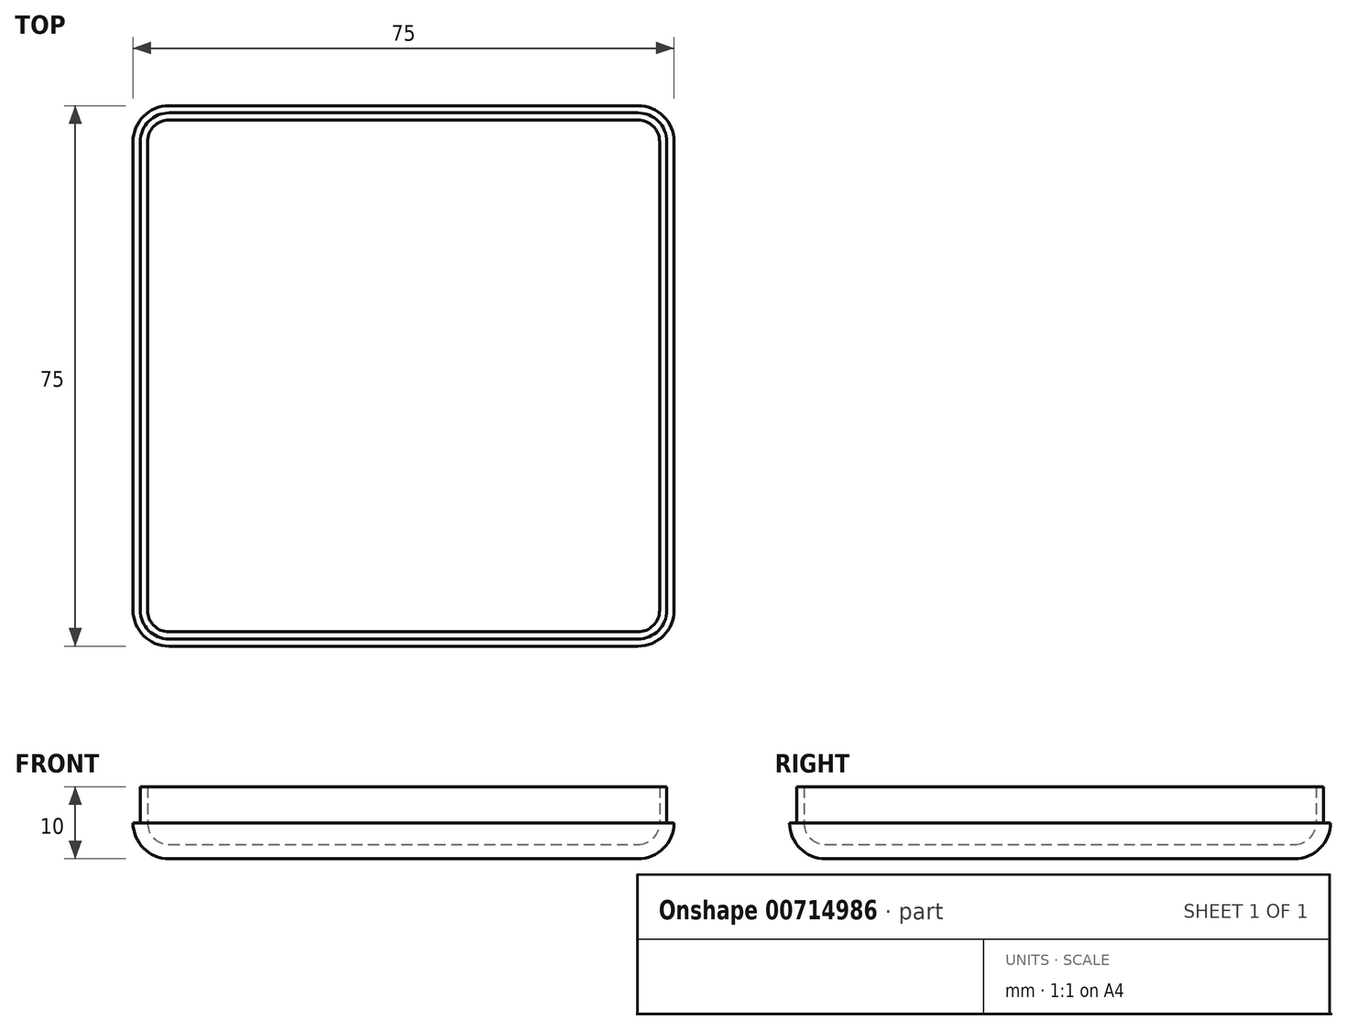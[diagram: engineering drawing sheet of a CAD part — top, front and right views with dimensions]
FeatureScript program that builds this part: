
annotation { "Feature Type Name" : "Feature", "Feature Type Description" : "" }
export const myFeature = defineFeature(function(context is Context, id is Id, definition is map)
    precondition{}
    {
        {
            var Q0;
            Q0=qCreatedBy(makeId("Top.planeOp"),FACE);
            var sketch = newSketch(context, id + "F0", { "sketchPlane" : qUnion([Q0])});
            skLineSegment(sketch, "E0.bottom", {"start": v(-37.5, 37.5) * mm, "end": v(37.5, 37.5) * mm});
            skLineSegment(sketch, "E0.top", {"start": v(-37.5, -37.5) * mm, "end": v(37.5, -37.5) * mm});
            skLineSegment(sketch, "E0.left", {"start": v(-37.5, 37.5) * mm, "end": v(-37.5, -37.5) * mm});
            skLineSegment(sketch, "E0.right", {"start": v(37.5, 37.5) * mm, "end": v(37.5, -37.5) * mm});
            skPoint(sketch, "E0.middle", {"position": v(0, 0) * mm});
            skLineSegment(sketch, "E1.0", {"start": v(-35.5, 35.5) * mm, "end": v(35.5, 35.5) * mm});
            skLineSegment(sketch, "E1.1", {"start": v(-35.5, 35.5) * mm, "end": v(-35.5, -35.5) * mm});
            skLineSegment(sketch, "E1.2", {"start": v(-35.5, -35.5) * mm, "end": v(35.5, -35.5) * mm});
            skLineSegment(sketch, "E1.3", {"start": v(35.5, 35.5) * mm, "end": v(35.5, -35.5) * mm});
            skSolve(sketch);
        }
        {
            var Q0;
            Q0=makeQuery(id+"F0.imprint","IMPRINT",FACE,{"disambiguationData":[TD([[makeQuery(id+"F0.imprint","IMPRINT",EDGE,{"derivedFrom":sQuery(id+"F0.wireOp",EDGE,"E1.0")}),-1.0]])]});
            var Q1;
            Q1=makeQuery(id+"F0.imprint","IMPRINT",FACE,{"disambiguationData":[TD([[makeQuery(id+"F0.imprint","IMPRINT",EDGE,{"derivedFrom":sQuery(id+"F0.wireOp",EDGE,"E0.bottom")}),-1.0]])]});
            extrude(context, id + "F1", {"entities" : qUnion([Q0, Q1]), "depth" : 5 * mm, "offsetDistance" : 25 * mm});
        }
        {
            var Q0;
            Q0=makeQuery(id+"F1.opExtrude","SWEPT_EDGE",EDGE,{"disambiguationData":[OSD([sQuery(id+"F0.wireOp",EDGE,"E0.top"),sQuery(id+"F0.wireOp",EDGE,"E0.left")])]});
            var Q1;
            Q1=makeQuery(id+"F1.opExtrude","SWEPT_EDGE",EDGE,{"disambiguationData":[OSD([sQuery(id+"F0.wireOp",EDGE,"E0.top"),sQuery(id+"F0.wireOp",EDGE,"E0.right")])]});
            var Q2;
            Q2=makeQuery(id+"F1.opExtrude","CAP_EDGE",EDGE,{"disambiguationData":[OSD([sQuery(id+"F0.wireOp",EDGE,"E0.top")])],"isStart":true});
            var Q3;
            Q3=makeQuery(id+"F1.opExtrude","CAP_EDGE",EDGE,{"disambiguationData":[OSD([sQuery(id+"F0.wireOp",EDGE,"E0.left")])],"isStart":true});
            var Q4;
            Q4=makeQuery(id+"F1.opExtrude","SWEPT_EDGE",EDGE,{"disambiguationData":[OSD([sQuery(id+"F0.wireOp",EDGE,"E0.bottom"),sQuery(id+"F0.wireOp",EDGE,"E0.left")])]});
            var Q5;
            Q5=makeQuery(id+"F1.opExtrude","CAP_EDGE",EDGE,{"disambiguationData":[OSD([sQuery(id+"F0.wireOp",EDGE,"E0.bottom")])],"isStart":true});
            var Q6;
            Q6=makeQuery(id+"F1.opExtrude","SWEPT_EDGE",EDGE,{"disambiguationData":[OSD([sQuery(id+"F0.wireOp",EDGE,"E0.bottom"),sQuery(id+"F0.wireOp",EDGE,"E0.right")])]});
            var Q7;
            Q7=makeQuery(id+"F1.opExtrude","CAP_EDGE",EDGE,{"disambiguationData":[OSD([sQuery(id+"F0.wireOp",EDGE,"E0.right")])],"isStart":true});
            fillet(context, id + "F2", {"entities" : qUnion([Q0, Q1, Q2, Q3, Q4, Q5, Q6, Q7]), "radius" : 5 * mm, "tangentPropagation" : true, "allowEdgeOverflow" : false});
        }
        {
            var Q0;
            Q0=makeQuery(id+"F1.opExtrude","CAP_FACE",FACE,{"disambiguationData":[OSD([sQuery(id+"F0.wireOp",EDGE,"E0.bottom"),sQuery(id+"F0.wireOp",EDGE,"E0.top"),sQuery(id+"F0.wireOp",EDGE,"E0.left"),sQuery(id+"F0.wireOp",EDGE,"E0.right")])],"isStart":false});
            shell(context, id + "F3", {"entities" : qUnion([Q0]), "thickness" : 2 * mm});
        }
        {
            var Q0;
            Q0=makeQuery(id+"F1.opExtrude","CAP_FACE",FACE,{"disambiguationData":[OSD([sQuery(id+"F0.wireOp",EDGE,"E0.bottom"),sQuery(id+"F0.wireOp",EDGE,"E0.top"),sQuery(id+"F0.wireOp",EDGE,"E0.left"),sQuery(id+"F0.wireOp",EDGE,"E0.right")])],"isStart":false});
            cPlane(context, id + "F4", {"entities" : qUnion([Q0]), "cplaneType" : CPlaneType.OFFSET, "offset" : 0 * mm, "width" : 150 * mm, "height" : 150 * mm});
        }
        {
            var Q0;
            Q0=qCreatedBy(id+"F4.planeOp",FACE);
            var sketch = newSketch(context, id + "F5", { "sketchPlane" : qUnion([Q0])});
            skArc(sketch, "E2.0", {"start": v(-36.5, -32.5) * mm, "mid": v(-35.33, -35.33) * mm, "end": v(-32.5, -36.5) * mm});
            skLineSegment(sketch, "E2.1", {"start": v(-36.5, 32.5) * mm, "end": v(-36.5, -32.5) * mm});
            skLineSegment(sketch, "E2.2", {"start": v(-32.5, -36.5) * mm, "end": v(32.5, -36.5) * mm});
            skArc(sketch, "E2.3", {"start": v(-32.5, 36.5) * mm, "mid": v(-35.33, 35.33) * mm, "end": v(-36.5, 32.5) * mm});
            skArc(sketch, "E2.4", {"start": v(32.5, -36.5) * mm, "mid": v(35.33, -35.33) * mm, "end": v(36.5, -32.5) * mm});
            skLineSegment(sketch, "E2.5", {"start": v(36.5, 32.5) * mm, "end": v(36.5, -32.5) * mm});
            skArc(sketch, "E2.6", {"start": v(36.5, 32.5) * mm, "mid": v(35.33, 35.33) * mm, "end": v(32.5, 36.5) * mm});
            skLineSegment(sketch, "E2.7", {"start": v(-32.5, 36.5) * mm, "end": v(32.5, 36.5) * mm});
            skLineSegment(sketch, "E3.0", {"start": v(-32.5, 35.5) * mm, "end": v(32.5, 35.5) * mm});
            skArc(sketch, "E4.0", {"start": v(35.5, 32.5) * mm, "mid": v(34.62, 34.62) * mm, "end": v(32.5, 35.5) * mm});
            skLineSegment(sketch, "E5.0", {"start": v(35.5, 32.5) * mm, "end": v(35.5, -32.5) * mm});
            skArc(sketch, "E6.0", {"start": v(32.5, -35.5) * mm, "mid": v(34.62, -34.62) * mm, "end": v(35.5, -32.5) * mm});
            skLineSegment(sketch, "E7.0", {"start": v(-32.5, -35.5) * mm, "end": v(32.5, -35.5) * mm});
            skArc(sketch, "E8.0", {"start": v(-35.5, -32.5) * mm, "mid": v(-34.62, -34.62) * mm, "end": v(-32.5, -35.5) * mm});
            skLineSegment(sketch, "E9.0", {"start": v(-35.5, 32.5) * mm, "end": v(-35.5, -32.5) * mm});
            skArc(sketch, "E10.0", {"start": v(-32.5, 35.5) * mm, "mid": v(-34.62, 34.62) * mm, "end": v(-35.5, 32.5) * mm});
            skSolve(sketch);
        }
        {
            var Q0;
            Q0=makeQuery(id+"F5.imprint","IMPRINT",FACE,{"disambiguationData":[TD([[makeQuery(id+"F5.imprint","IMPRINT",EDGE,{"derivedFrom":sQuery(id+"F5.wireOp",EDGE,"E2.0")}),1.0]])]});
            extrude(context, id + "F6", {"entities" : qUnion([Q0]), "operationType" : NewBodyOperationType.ADD, "depth" : 5 * mm, "offsetDistance" : 25 * mm});
        }
        {
            var Q0;
            Q0=qCreatedBy(makeId("Top.planeOp"),FACE);
            var sketch = newSketch(context, id + "F7", { "sketchPlane" : qUnion([Q0])});
            skLineSegment(sketch, "E11", {"start": v(0, -41.9) * mm, "end": v(0, 56.18) * mm, "construction": true});
            skSolve(sketch);
        }
        {
            var Q0;
            Q0=makeQuery(id+"F1.opExtrude","SWEPT_BODY",BODY,{"disambiguationData":[OSD([sQuery(id+"F0.wireOp",EDGE,"E0.bottom"),sQuery(id+"F0.wireOp",EDGE,"E0.top"),sQuery(id+"F0.wireOp",EDGE,"E0.left"),sQuery(id+"F0.wireOp",EDGE,"E0.right")])]});
            var Q1;
            Q1=sQuery(id+"F7.wireOp",EDGE,"E11");
            transform(context, id + "F8", {"entities" : qUnion([Q0]), "transformType" : TransformType.ROTATION, "transformAxis" : qUnion([Q1]), "angle" : 180 * degree, "makeCopy" : false});
        }
        {
            var Q0;
            Q0=makeQuery(id+"F1.opExtrude","SWEPT_BODY",BODY,{"disambiguationData":[OSD([sQuery(id+"F0.wireOp",EDGE,"E0.bottom"),sQuery(id+"F0.wireOp",EDGE,"E0.top"),sQuery(id+"F0.wireOp",EDGE,"E0.left"),sQuery(id+"F0.wireOp",EDGE,"E0.right")])]});
            transform(context, id + "F9", {"entities" : qUnion([Q0]), "transformType" : TransformType.TRANSLATION_3D, "dx" : 0 * mm, "dy" : 0 * mm, "dz" : 7.5 * mm, "makeCopy" : false});
        }
        {
            var Q0;
            Q0=qCreatedBy(id+"F4.planeOp",FACE);
            cPlane(context, id + "F10", {"entities" : qUnion([Q0]), "cplaneType" : CPlaneType.OFFSET, "offset" : 2.5 * mm, "width" : 150 * mm, "height" : 150 * mm});
        }
        {
            var Q0;
            Q0=makeQuery(id+"F1.opExtrude","SWEPT_BODY",BODY,{"disambiguationData":[OSD([sQuery(id+"F0.wireOp",EDGE,"E0.bottom"),sQuery(id+"F0.wireOp",EDGE,"E0.top"),sQuery(id+"F0.wireOp",EDGE,"E0.left"),sQuery(id+"F0.wireOp",EDGE,"E0.right")])]});
            var Q1;
            Q1=sQuery(id+"F7.wireOp",EDGE,"E11");
            transform(context, id + "F11", {"entities" : qUnion([Q0]), "transformType" : TransformType.ROTATION, "transformAxis" : qUnion([Q1]), "angle" : 180 * degree, "makeCopy" : false});
        }
        {
            var Q0;
            Q0=makeQuery(id+"F1.opExtrude","SWEPT_BODY",BODY,{"disambiguationData":[OSD([sQuery(id+"F0.wireOp",EDGE,"E0.bottom"),sQuery(id+"F0.wireOp",EDGE,"E0.top"),sQuery(id+"F0.wireOp",EDGE,"E0.left"),sQuery(id+"F0.wireOp",EDGE,"E0.right")])]});
            transform(context, id + "F12", {"entities" : qUnion([Q0]), "transformType" : TransformType.TRANSLATION_3D, "dx" : 0 * mm, "dy" : 0 * mm, "dz" : 7.6 * mm, "makeCopy" : false});
        }
        {
            var Q0;
            Q0=makeQuery(id+"F1.opExtrude","SWEPT_BODY",BODY,{"disambiguationData":[OSD([sQuery(id+"F0.wireOp",EDGE,"E0.bottom"),sQuery(id+"F0.wireOp",EDGE,"E0.top"),sQuery(id+"F0.wireOp",EDGE,"E0.left"),sQuery(id+"F0.wireOp",EDGE,"E0.right")])]});
            transform(context, id + "F13", {"entities" : qUnion([Q0]), "transformType" : TransformType.TRANSLATION_3D, "dx" : 0 * mm, "dy" : 0 * mm, "dz" : -0.09 * mm, "makeCopy" : false});
        }
        {
            var Q0;
            Q0=makeQuery(id+"F1.opExtrude","SWEPT_BODY",BODY,{"disambiguationData":[OSD([sQuery(id+"F0.wireOp",EDGE,"E0.bottom"),sQuery(id+"F0.wireOp",EDGE,"E0.top"),sQuery(id+"F0.wireOp",EDGE,"E0.left"),sQuery(id+"F0.wireOp",EDGE,"E0.right")])]});
            transform(context, id + "F14", {"entities" : qUnion([Q0]), "transformType" : TransformType.TRANSLATION_3D, "dx" : 0 * mm, "dy" : 0 * mm, "dz" : -.1 * mm, "makeCopy" : false});
        }
    });
